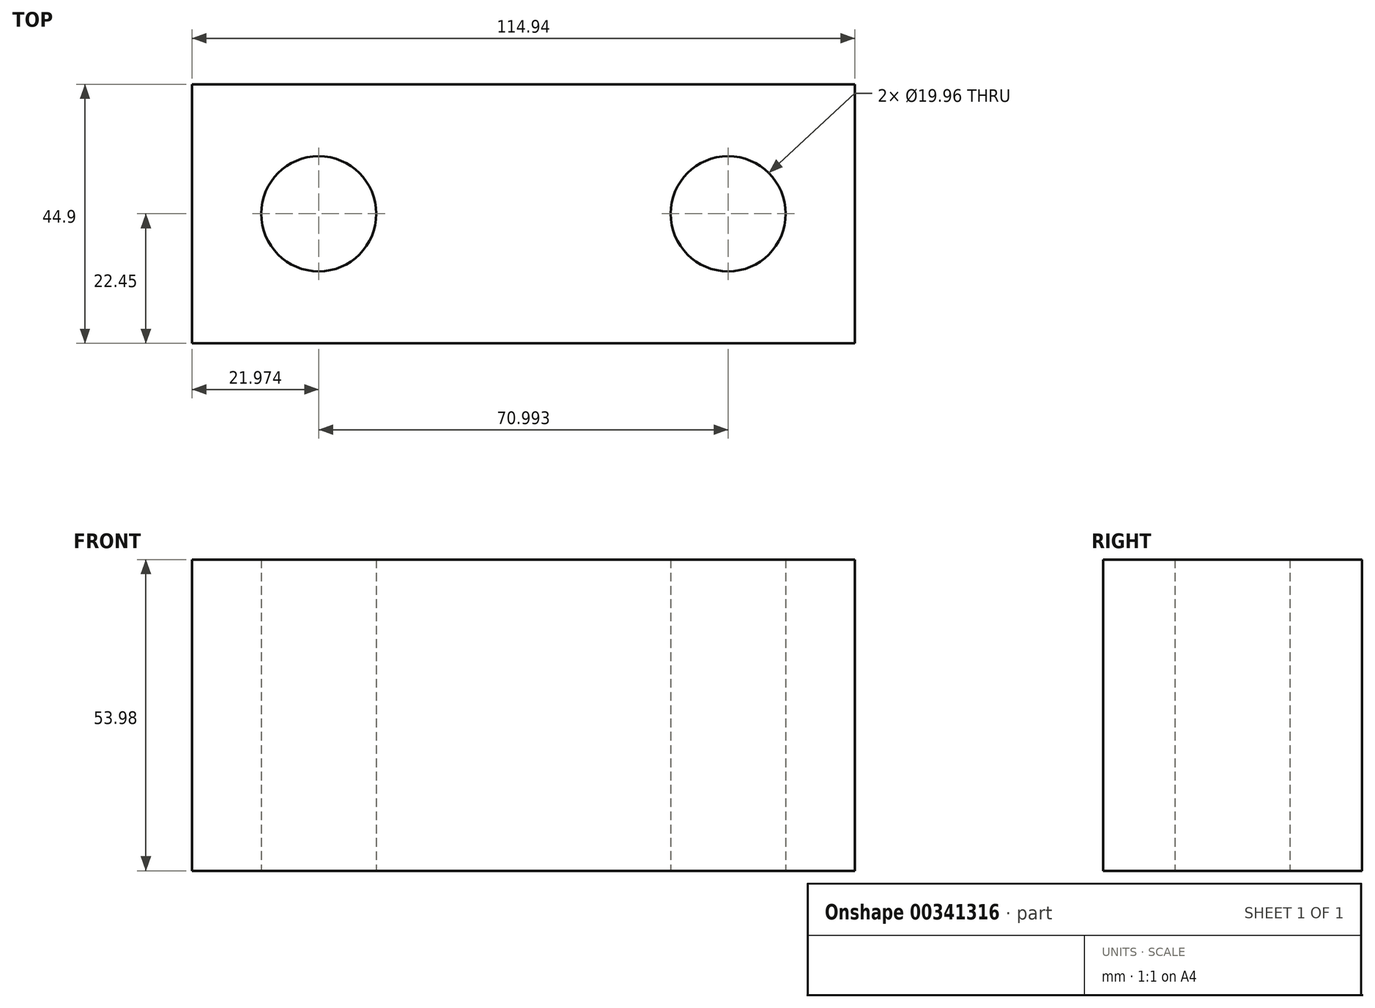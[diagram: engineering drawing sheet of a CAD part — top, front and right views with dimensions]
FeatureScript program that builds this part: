
annotation { "Feature Type Name" : "Feature", "Feature Type Description" : "" }
export const myFeature = defineFeature(function(context is Context, id is Id, definition is map)
    precondition{}
    {
        {
            var Q0;
            Q0=qCreatedBy(makeId("Top.planeOp"),FACE);
            var sketch = newSketch(context, id + "F0", { "sketchPlane" : qUnion([Q0])});
            skLineSegment(sketch, "E0.bottom", {"start": v(57.47, 22.45) * mm, "end": v(-57.47, 22.45) * mm});
            skLineSegment(sketch, "E0.top", {"start": v(57.47, -22.45) * mm, "end": v(-57.47, -22.45) * mm});
            skLineSegment(sketch, "E0.left", {"start": v(57.47, 22.45) * mm, "end": v(57.47, -22.45) * mm});
            skLineSegment(sketch, "E0.right", {"start": v(-57.47, 22.45) * mm, "end": v(-57.47, -22.45) * mm});
            skPoint(sketch, "E0.middle", {"position": v(0, 0) * mm});
            skCircle(sketch, "E1", {"center": v(-35.5, 0) * mm, "radius": 9.98 * mm});
            skCircle(sketch, "E2", {"center": v(35.5, 0) * mm, "radius": 9.98 * mm});
            skSolve(sketch);
        }
        {
            var Q0;
            Q0 = qSketchRegion(id + "F0", true);
            extrude(context, id + "F1", {"entities" : qUnion([Q0]), "depth" : 53.97 * mm});
        }
    });
